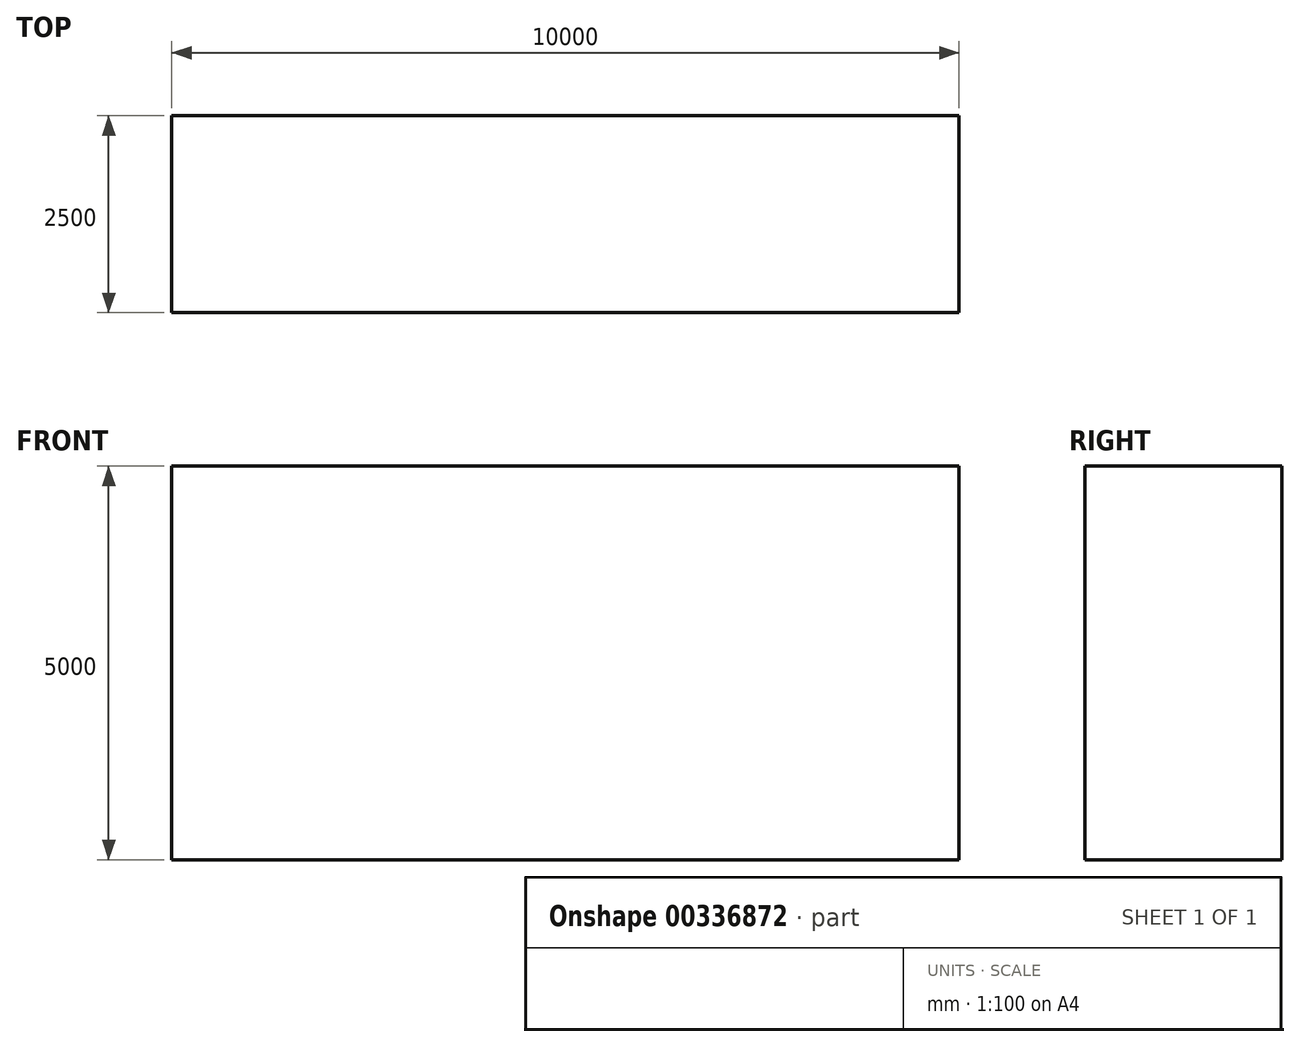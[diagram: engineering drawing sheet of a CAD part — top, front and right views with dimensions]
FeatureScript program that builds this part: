
annotation { "Feature Type Name" : "Feature", "Feature Type Description" : "" }
export const myFeature = defineFeature(function(context is Context, id is Id, definition is map)
    precondition{}
    {
        {
            var Q0;
            Q0=qCreatedBy(makeId("Front.planeOp"),FACE);
            var sketch = newSketch(context, id + "F0", { "sketchPlane" : qUnion([Q0])});
            skLineSegment(sketch, "E0.bottom", {"start": v(-4991.11, 2648.78) * mm, "end": v(5008.89, 2648.78) * mm});
            skLineSegment(sketch, "E0.top", {"start": v(-4991.11, -2351.22) * mm, "end": v(5008.89, -2351.22) * mm});
            skLineSegment(sketch, "E0.left", {"start": v(-4991.11, 2648.78) * mm, "end": v(-4991.11, -2351.22) * mm});
            skLineSegment(sketch, "E0.right", {"start": v(5008.89, 2648.78) * mm, "end": v(5008.89, -2351.22) * mm});
            skSolve(sketch);
        }
        {
            var Q0;
            Q0=makeQuery(id+"F0.imprint","IMPRINT",FACE,{"disambiguationData":[TD([[makeQuery(id+"F0.imprint","IMPRINT",EDGE,{"derivedFrom":sQuery(id+"F0.wireOp",EDGE,"E0.bottom")}),-1.0]])]});
            extrude(context, id + "F1", {"entities" : qUnion([Q0]), "depth" : 2500 * mm});
        }
    });
